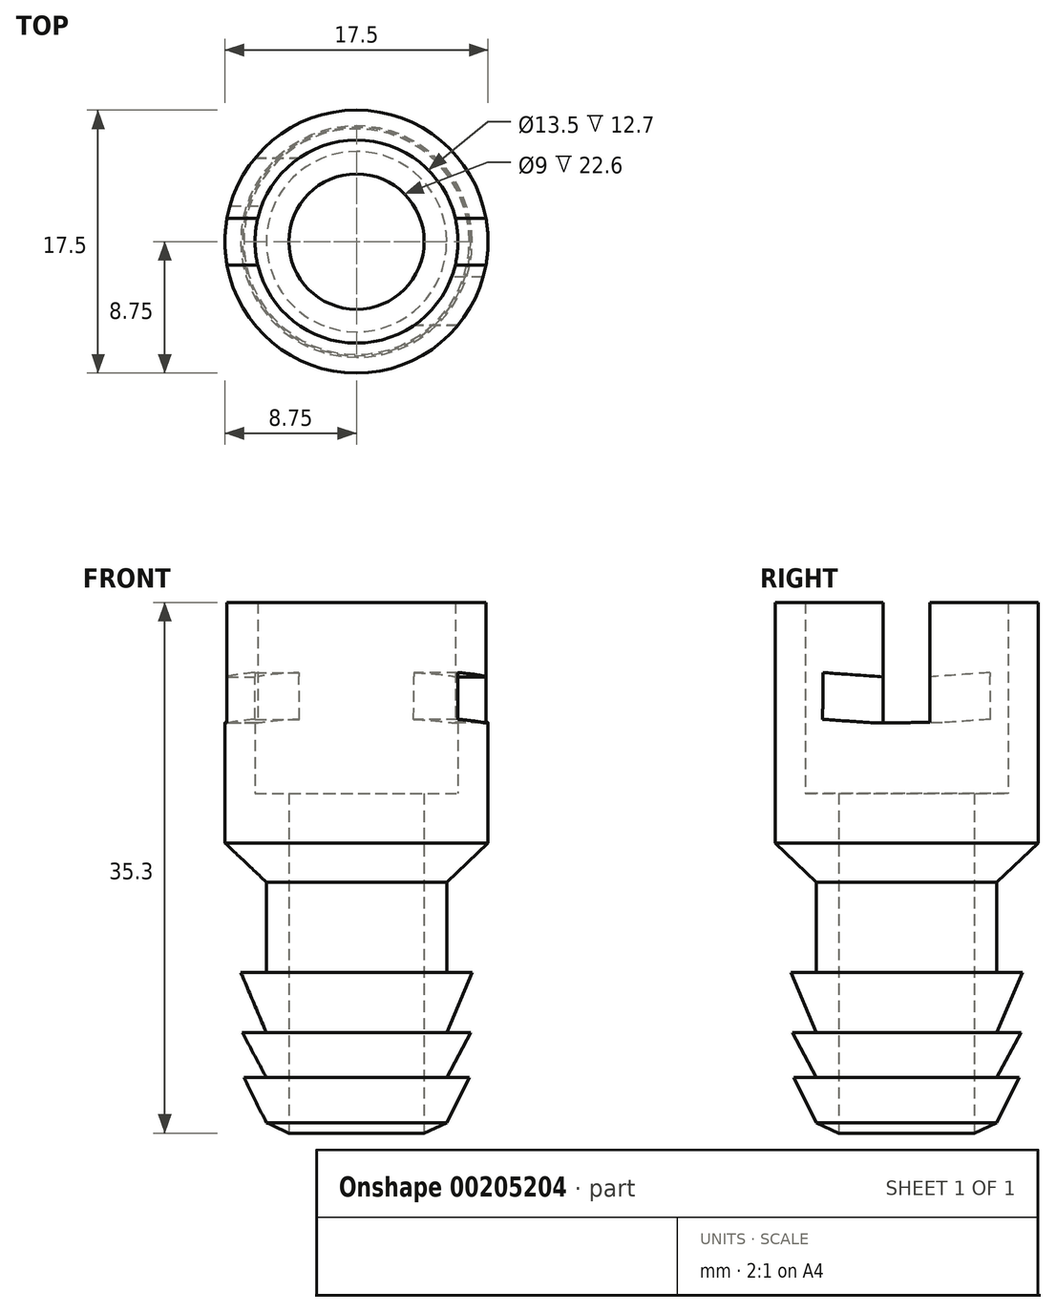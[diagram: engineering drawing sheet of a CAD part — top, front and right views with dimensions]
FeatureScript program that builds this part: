
annotation { "Feature Type Name" : "Feature", "Feature Type Description" : "" }
export const myFeature = defineFeature(function(context is Context, id is Id, definition is map)
    precondition{}
    {
        {
            var Q0;
            Q0=qCreatedBy(makeId("Right.planeOp"),FACE);
            var sketch = newSketch(context, id + "F0", { "sketchPlane" : qUnion([Q0])});
            skLineSegment(sketch, "E0", {"start": v(0, 0) * mm, "end": v(0, 28.24) * mm, "construction": true});
            skLineSegment(sketch, "E1", {"start": v(0, 0) * mm, "end": v(4.5, 0) * mm, "construction": true});
            skLineSegment(sketch, "E2", {"start": v(6.75, 4) * mm, "end": v(6.75, 16) * mm});
            skLineSegment(sketch, "E3", {"start": v(6.75, 16) * mm, "end": v(8.75, 16) * mm});
            skLineSegment(sketch, "E4", {"start": v(8.75, 16) * mm, "end": v(8.75, 0) * mm});
            skLineSegment(sketch, "E5", {"start": v(4.5, -19.3) * mm, "end": v(4.5, 0) * mm});
            skLineSegment(sketch, "E6", {"start": v(6, -2.6) * mm, "end": v(6, -8.6) * mm});
            skLineSegment(sketch, "E7", {"start": v(6, -8.6) * mm, "end": v(6, -2.6) * mm});
            skLineSegment(sketch, "E8", {"start": v(6, -15.6) * mm, "end": v(7.5, -15.6) * mm});
            skLineSegment(sketch, "E9", {"start": v(7.5, -15.6) * mm, "end": v(6, -18.6) * mm});
            skLineSegment(sketch, "E10", {"start": v(8.75, 0) * mm, "end": v(6, -2.6) * mm});
            skLineSegment(sketch, "E11", {"start": v(6, -18.6) * mm, "end": v(4.5, -19.3) * mm});
            skLineSegment(sketch, "E12", {"start": v(6.75, 4) * mm, "end": v(6.75, 3.3) * mm});
            skLineSegment(sketch, "E13", {"start": v(6.75, 3.3) * mm, "end": v(4.5, 3.3) * mm});
            skLineSegment(sketch, "E14", {"start": v(4.5, 3.3) * mm, "end": v(4.5, 0) * mm});
            skLineSegment(sketch, "E15", {"start": v(6, -8.6) * mm, "end": v(7.7, -8.6) * mm});
            skLineSegment(sketch, "E16", {"start": v(7.7, -8.6) * mm, "end": v(6, -12.6) * mm});
            skLineSegment(sketch, "E17", {"start": v(6, -12.6) * mm, "end": v(7.6, -12.6) * mm});
            skLineSegment(sketch, "E18", {"start": v(7.6, -12.6) * mm, "end": v(6, -15.6) * mm});
            skSolve(sketch);
        }
        {
            var Q0;
            Q0=makeQuery(id+"F0.imprint","IMPRINT",FACE,{"disambiguationData":[TD([[makeQuery(id+"F0.imprint","IMPRINT",EDGE,{"derivedFrom":sQuery(id+"F0.wireOp",EDGE,"E2")}),-1.0]])]});
            var Q1;
            Q1=sQuery(id+"F0.wireOp",EDGE,"E0");
            revolve(context, id + "F1", {"entities" : qUnion([Q0]), "axis" : qUnion([Q1]), "revolveType" : RevolveType.FULL});
        }
        {
            var Q0;
            Q0=qCreatedBy(makeId("Right.planeOp"),FACE);
            var sketch = newSketch(context, id + "F2", { "sketchPlane" : qUnion([Q0])});
            skLineSegment(sketch, "E19.right", {"start": v(-1.55, 8) * mm, "end": v(-1.55, 16.1) * mm});
            skLineSegment(sketch, "E20.right", {"start": v(-5.58, 8.23) * mm, "end": v(-5.56, 11.07) * mm});
            skLineSegment(sketch, "E21", {"start": v(-5.56, 11.07) * mm, "end": v(-5.56, 11.33) * mm});
            skLineSegment(sketch, "E22", {"start": v(-5.56, 11.33) * mm, "end": v(-1.55, 11.05) * mm});
            skLineSegment(sketch, "E23.0", {"start": v(-5.58, 8.23) * mm, "end": v(-2.37, 8) * mm});
            skLineSegment(sketch, "E24.MirrorCS", {"start": v(1.55, 8.01) * mm, "end": v(1.55, 16.1) * mm});
            skLineSegment(sketch, "E25", {"start": v(0, 9.29) * mm, "end": v(0, 4.95) * mm, "construction": true});
            skLineSegment(sketch, "E26", {"start": v(-1.55, 16.1) * mm, "end": v(1.55, 16.1) * mm});
            skLineSegment(sketch, "E27", {"start": v(-1.55, 11.05) * mm, "end": v(-1.55, 8) * mm});
            skLineSegment(sketch, "E28", {"start": v(-1.55, 8) * mm, "end": v(1.55, 8.01) * mm});
            skLineSegment(sketch, "E29", {"start": v(1.55, 16.1) * mm, "end": v(1.55, 8.01) * mm});
            skLineSegment(sketch, "E30", {"start": v(-2.37, 8) * mm, "end": v(-1.55, 8) * mm});
            skLineSegment(sketch, "E31.MirrorCS", {"start": v(1.55, 11.05) * mm, "end": v(1.55, 8) * mm});
            skLineSegment(sketch, "E32.MirrorCS", {"start": v(5.56, 11.33) * mm, "end": v(1.55, 11.05) * mm});
            skLineSegment(sketch, "E33.MirrorCS", {"start": v(5.56, 11.07) * mm, "end": v(5.56, 11.33) * mm});
            skLineSegment(sketch, "E34.MirrorCS", {"start": v(5.58, 8.23) * mm, "end": v(5.56, 11.07) * mm});
            skLineSegment(sketch, "E35.MirrorCS", {"start": v(5.58, 8.23) * mm, "end": v(2.37, 8) * mm});
            skLineSegment(sketch, "E36.MirrorCS", {"start": v(2.37, 8) * mm, "end": v(1.55, 8) * mm});
            skSolve(sketch);
        }
        {
            var Q0;
            Q0=makeQuery(id+"F2.imprint","IMPRINT",FACE,{"disambiguationData":[TD([[makeQuery(id+"F2.imprint","IMPRINT",EDGE,{"derivedFrom":sQuery(id+"F2.wireOp",EDGE,"E19.right")}),-1.0]])]});
            var Q1;
            Q1=makeQuery(id+"F2.imprint","IMPRINT",FACE,{"disambiguationData":[TD([[makeQuery(id+"F2.imprint","IMPRINT",EDGE,{"derivedFrom":sQuery(id+"F2.wireOp",EDGE,"E20.right")}),-1.0]])]});
            var Q2;
            Q2=sQuery(id+"F2.wireOp",EDGE,"E22");
            extrude(context, id + "F3", {"entities" : qUnion([Q0, Q1]), "operationType" : NewBodyOperationType.REMOVE, "surfaceEntities" : qUnion([Q2]), "depth" : 25 * mm});
        }
        {
            var Q0;
            {var subQ0=sQuery(id+"F2.wireOp",EDGE,"E32.MirrorCS");Q0=makeQuery(id+"F2.imprint","IMPRINT",FACE,{"disambiguationData":[TD([[makeQuery(id+"F2.imprint","IMPRINT",EDGE,{"derivedFrom":subQ0}),1.0]])]});}
            var Q1;
            Q1=makeQuery(id+"F2.imprint","IMPRINT",FACE,{"disambiguationData":[TD([[makeQuery(id+"F2.imprint","IMPRINT",EDGE,{"derivedFrom":sQuery(id+"F2.wireOp",EDGE,"E19.right")}),-1.0]])]});
            var Q2;
            Q2=sQuery(id+"F2.wireOp",EDGE,"334bf0be-a9da-4ac8-bafd-b2634f9c0df80.MirrorCS");
            var Q3;
            Q3=sQuery(id+"F2.wireOp",EDGE,"1f5feb23-1326-47c1-b2c3-2211c469e6ca0.MirrorCS");
            var Q4;
            Q4=sQuery(id+"F2.wireOp",EDGE,"60578f22-4a36-44cc-9bdb-ccab681199b60.MirrorCS");
            var Q5;
            Q5=sQuery(id+"F2.wireOp",EDGE,"3c4da9f2-6952-45a1-970b-3157558d97f10.MirrorCS");
            var Q6;
            Q6=sQuery(id+"F2.wireOp",EDGE,"bjV3OR7o-xhmJ-dWGn-PfCg-U56WJ0KrUroz");
            var Q7;
            Q7=sQuery(id+"F2.wireOp",EDGE,"E24.MirrorCS");
            var Q8;
            Q8=sQuery(id+"F2.wireOp",EDGE,"YNu7n84e-Eg7w-5ggM-8PGD-B6xNwlmQT34N");
            var Q9;
            Q9=sQuery(id+"F2.wireOp",EDGE,"Ne00rjo2-OPhW-Emyz-FI9t-viegDZjm54rB");
            extrude(context, id + "F4", {"entities" : qUnion([Q0, Q1]), "operationType" : NewBodyOperationType.REMOVE, "surfaceEntities" : qUnion([Q2, Q3, Q4, Q5, Q6, Q7, Q8, Q9]), "oppositeDirection" : true, "depth" : 25 * mm});
        }
    });
